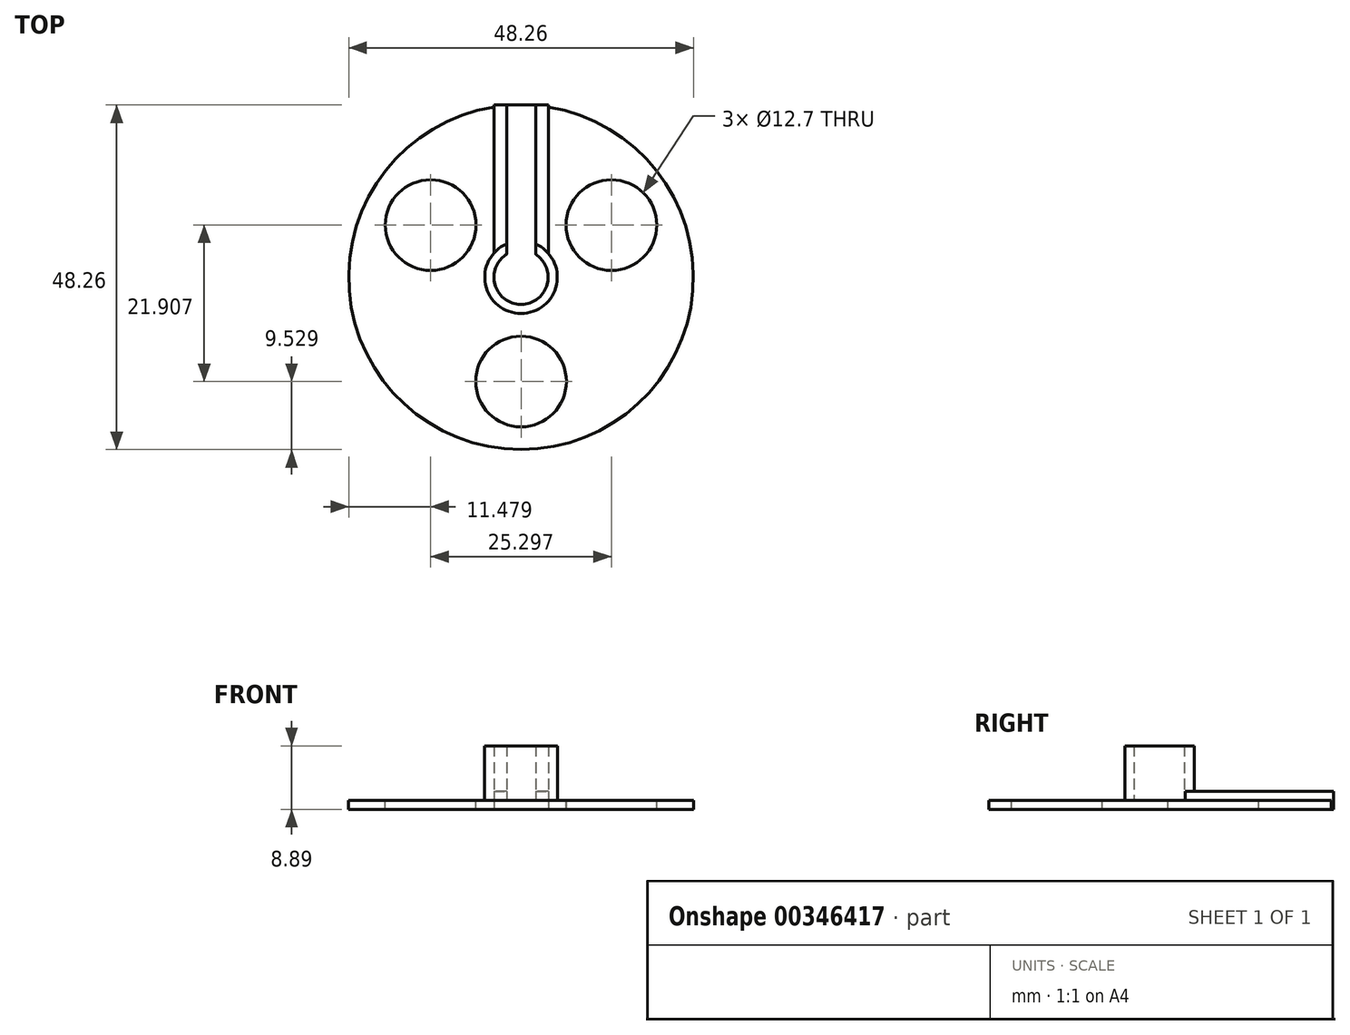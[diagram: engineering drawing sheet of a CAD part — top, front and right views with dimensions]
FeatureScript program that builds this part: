
annotation { "Feature Type Name" : "Feature", "Feature Type Description" : "" }
export const myFeature = defineFeature(function(context is Context, id is Id, definition is map)
    precondition{}
    {
        {
            var Q0;
            Q0=qCreatedBy(makeId("Top.planeOp"),FACE);
            var sketch = newSketch(context, id + "F0", { "sketchPlane" : qUnion([Q0])});
            skLineSegment(sketch, "E0.bottom", {"start": v(-94.86, 41.16) * mm, "end": v(-87.24, 41.16) * mm});
            skLineSegment(sketch, "E0.top", {"start": v(-94.86, 17.03) * mm, "end": v(-87.24, 17.03) * mm});
            skLineSegment(sketch, "E0.left", {"start": v(-94.86, 41.16) * mm, "end": v(-94.86, 17.03) * mm});
            skLineSegment(sketch, "E0.right", {"start": v(-87.24, 41.16) * mm, "end": v(-87.24, 17.03) * mm});
            skSolve(sketch);
        }
        {
            var Q0;
            Q0 = qSketchRegion(id + "F0", true);
            extrude(context, id + "F1", {"entities" : qUnion([Q0]), "depth" : 1.27 * mm});
        }
        {
            var Q0;
            Q0=makeQuery(id+"F1.opExtrude","CAP_FACE",FACE,{"disambiguationData":[OSD([sQuery(id+"F0.wireOp",EDGE,"E0.bottom"),sQuery(id+"F0.wireOp",EDGE,"E0.top"),sQuery(id+"F0.wireOp",EDGE,"E0.left"),sQuery(id+"F0.wireOp",EDGE,"E0.right")])],"isStart":false});
            var sketch = newSketch(context, id + "F2", { "sketchPlane" : qUnion([Q0])});
            skLineSegment(sketch, "E1.bottom", {"start": v(-94.86, 41.16) * mm, "end": v(-93.08, 41.16) * mm});
            skLineSegment(sketch, "E1.top", {"start": v(-94.86, 17.03) * mm, "end": v(-93.08, 17.03) * mm});
            skLineSegment(sketch, "E1.left", {"start": v(-94.86, 41.16) * mm, "end": v(-94.86, 17.03) * mm});
            skLineSegment(sketch, "E1.right", {"start": v(-93.08, 41.16) * mm, "end": v(-93.08, 17.03) * mm});
            skLineSegment(sketch, "E2.bottom", {"start": v(-87.24, 41.16) * mm, "end": v(-89.02, 41.16) * mm});
            skLineSegment(sketch, "E2.top", {"start": v(-87.24, 17.03) * mm, "end": v(-89.02, 17.03) * mm});
            skLineSegment(sketch, "E2.left", {"start": v(-87.24, 41.16) * mm, "end": v(-87.24, 17.03) * mm});
            skLineSegment(sketch, "E2.right", {"start": v(-89.02, 41.16) * mm, "end": v(-89.02, 17.03) * mm});
            skSolve(sketch);
        }
        {
            var Q0;
            Q0 = qSketchRegion(id + "F2", true);
            extrude(context, id + "F3", {"entities" : qUnion([Q0]), "operationType" : NewBodyOperationType.ADD, "depth" : 1.27 * mm});
        }
        {
            var Q0;
            Q0=makeQuery(id+"F1.opExtrude","CAP_FACE",FACE,{"disambiguationData":[OSD([sQuery(id+"F0.wireOp",EDGE,"E0.bottom"),sQuery(id+"F0.wireOp",EDGE,"E0.top"),sQuery(id+"F0.wireOp",EDGE,"E0.left"),sQuery(id+"F0.wireOp",EDGE,"E0.right")])],"isStart":false});
            var sketch = newSketch(context, id + "F4", { "sketchPlane" : qUnion([Q0])});
            skCircle(sketch, "E3", {"center": v(-91.05, 17.03) * mm, "radius": 5.08 * mm});
            skSolve(sketch);
        }
        {
            var Q0;
            Q0 = qSketchRegion(id + "F4", true);
            var Q1;
            Q1=makeQuery(id+"F1.opExtrude","CAP_FACE",FACE,{"disambiguationData":[OSD([sQuery(id+"F0.wireOp",EDGE,"E0.bottom"),sQuery(id+"F0.wireOp",EDGE,"E0.top"),sQuery(id+"F0.wireOp",EDGE,"E0.left"),sQuery(id+"F0.wireOp",EDGE,"E0.right")])],"isStart":true});
            extrude(context, id + "F5", {"entities" : qUnion([Q0]), "operationType" : NewBodyOperationType.ADD, "depth" : 7.62 * mm, "hasSecondDirection" : true, "secondDirectionBound" : SecondDirectionBoundingType.UP_TO_SURFACE, "secondDirectionOppositeDirection" : true, "secondDirectionBoundEntityFace" : qUnion([Q1]), "secondDirectionDepth" : 25.4 * mm});
        }
        {
            var Q0;
            Q0=makeQuery(id+"F5.opExtrude","CAP_FACE",FACE,{"disambiguationData":[OSD([sQuery(id+"F4.wireOp",EDGE,"E3")])],"isStart":false});
            shell(context, id + "F6", {"entities" : qUnion([Q0]), "thickness" : 1.27 * mm});
        }
        {
            var Q0;
            Q0=makeQuery(id+"F3.boolean.opBoolean","MERGE",FACE,{"derivedFrom":[makeQuery(id+"F1.opExtrude","SWEPT_FACE",FACE,{"disambiguationData":[OSD([sQuery(id+"F0.wireOp",EDGE,"E0.bottom")])]}),makeQuery(id+"F3.opExtrude","SWEPT_FACE",FACE,{"disambiguationData":[OSD([sQuery(id+"F2.wireOp",EDGE,"E1.bottom")])]}),makeQuery(id+"F3.opExtrude","SWEPT_FACE",FACE,{"disambiguationData":[OSD([sQuery(id+"F2.wireOp",EDGE,"E2.bottom")])]})]});
            var sketch = newSketch(context, id + "F7", { "sketchPlane" : qUnion([Q0])});
            skLineSegment(sketch, "E4.bottom", {"start": v(93.08, 2.54) * mm, "end": v(89.02, 2.54) * mm});
            skLineSegment(sketch, "E4.top", {"start": v(93.08, 1.27) * mm, "end": v(89.02, 1.27) * mm});
            skLineSegment(sketch, "E4.left", {"start": v(93.08, 2.54) * mm, "end": v(93.08, 1.27) * mm});
            skLineSegment(sketch, "E4.right", {"start": v(89.02, 2.54) * mm, "end": v(89.02, 1.27) * mm});
            skSolve(sketch);
        }
        {
            var Q0;
            Q0 = qSketchRegion(id + "F7", true);
            var Q1;
            {var subQ1=sQuery(id+"F2.wireOp",EDGE,"E1.top");var subQ2=sQuery(id+"F0.wireOp",EDGE,"E0.left");var subQ4=sQuery(id+"F0.wireOp",EDGE,"E0.top");Q1=makeQuery(id+"F5.boolean.opBoolean","SPLIT",FACE,{"disambiguationData":[TD([makeQuery(id+"F1.opExtrude","SWEPT_FACE",FACE,{"disambiguationData":[OSD([subQ2])]})])],"derivedFrom":makeQuery(id+"F3.boolean.opBoolean","MERGE",FACE,{"derivedFrom":[makeQuery(id+"F1.opExtrude","SWEPT_FACE",FACE,{"disambiguationData":[OSD([subQ4])]}),makeQuery(id+"F3.opExtrude","SWEPT_FACE",FACE,{"disambiguationData":[OSD([subQ1])]}),makeQuery(id+"F3.opExtrude","SWEPT_FACE",FACE,{"disambiguationData":[OSD([sQuery(id+"F2.wireOp",EDGE,"E2.top")])]})]})});}
            extrude(context, id + "F8", {"entities" : qUnion([Q0]), "operationType" : NewBodyOperationType.REMOVE, "oppositeDirection" : true, "endBoundEntityFace" : qUnion([Q1]), "depth" : 25.4 * mm});
        }
        {
            var Q0;
            Q0=makeQuery(id+"F3.boolean.opBoolean","MERGE",FACE,{"derivedFrom":[makeQuery(id+"F1.opExtrude","SWEPT_FACE",FACE,{"disambiguationData":[OSD([sQuery(id+"F0.wireOp",EDGE,"E0.bottom")])]}),makeQuery(id+"F3.opExtrude","SWEPT_FACE",FACE,{"disambiguationData":[OSD([sQuery(id+"F2.wireOp",EDGE,"E1.bottom")])]}),makeQuery(id+"F3.opExtrude","SWEPT_FACE",FACE,{"disambiguationData":[OSD([sQuery(id+"F2.wireOp",EDGE,"E2.bottom")])]})]});
            cPlane(context, id + "F9", {"entities" : qUnion([Q0]), "cplaneType" : CPlaneType.OFFSET, "offset" : 20.57 * mm, "oppositeDirection" : true, "width" : 152.4 * mm, "height" : 152.4 * mm});
        }
        {
            var Q0;
            Q0=qCreatedBy(id+"F9.planeOp",FACE);
            var sketch = newSketch(context, id + "F10", { "sketchPlane" : qUnion([Q0])});
            skLineSegment(sketch, "E5.0", {"start": v(89.02, 2.54) * mm, "end": v(93.08, 2.54) * mm});
            skArc(sketch, "E6", {"start": v(93.08, 2.54) * mm, "mid": v(91.05, 4.16) * mm, "end": v(89.02, 2.54) * mm});
            skSolve(sketch);
        }
        {
            var Q0;
            Q0 = qSketchRegion(id + "F10", true);
            extrude(context, id + "F11", {"entities" : qUnion([Q0]), "operationType" : NewBodyOperationType.REMOVE, "oppositeDirection" : true, "depth" : 2.54 * mm, "hasSecondDirection" : true, "secondDirectionOppositeDirection" : false, "secondDirectionDepth" : 2.54 * mm});
        }
        {
            var Q0;
            Q0=makeQuery(id+"F11.boolean.opBoolean","INTERSECT",EDGE,{"derivedFrom":[makeQuery(id+"F6.opShell","OFFSET_FACE",FACE,{"disambiguationData":[OSD([sQuery(id+"F4.wireOp",EDGE,"E3")])]}),makeQuery(id+"F11.opExtrude","SWEPT_FACE",FACE,{"disambiguationData":[OSD([sQuery(id+"F10.wireOp",EDGE,"E6")])]})]});
            fillet(context, id + "F12", {"entities" : qUnion([Q0]), "radius" : 2.54 * mm, "tangentPropagation" : true, "allowEdgeOverflow" : false});
        }
        {
            var Q0;
            Q0=makeQuery(id+"F5.boolean.opBoolean","MERGE",FACE,{"derivedFrom":[makeQuery(id+"F1.opExtrude","CAP_FACE",FACE,{"disambiguationData":[OSD([sQuery(id+"F0.wireOp",EDGE,"E0.bottom"),sQuery(id+"F0.wireOp",EDGE,"E0.top"),sQuery(id+"F0.wireOp",EDGE,"E0.left"),sQuery(id+"F0.wireOp",EDGE,"E0.right")])],"isStart":true}),makeQuery(id+"F5.opExtrude","CAP_FACE",FACE,{"disambiguationData":[OSD([sQuery(id+"F4.wireOp",EDGE,"E3")])],"isStart":true})]});
            var sketch = newSketch(context, id + "F13", { "sketchPlane" : qUnion([Q0])});
            skCircle(sketch, "E7", {"center": v(-91.05, -17.03) * mm, "radius": 24.13 * mm});
            skSolve(sketch);
        }
        {
            var Q0;
            Q0 = qSketchRegion(id + "F13", true);
            extrude(context, id + "F14", {"entities" : qUnion([Q0]), "operationType" : NewBodyOperationType.ADD, "oppositeDirection" : true, "depth" : 1.27 * mm});
        }
        {
            var Q0;
            Q0=makeQuery(id+"F14.opExtrude","CAP_FACE",FACE,{"disambiguationData":[OSD([sQuery(id+"F13.wireOp",EDGE,"E7")])],"isStart":false});
            var sketch = newSketch(context, id + "F15", { "sketchPlane" : qUnion([Q0])});
            skLineSegment(sketch, "E8.0", {"start": v(-87.24, 20.4) * mm, "end": v(-87.24, 40.86) * mm});
            skLineSegment(sketch, "E9", {"start": v(-91.05, 11.95) * mm, "end": v(-91.05, -7.1) * mm});
            skCircle(sketch, "E10", {"center": v(-91.05, 2.43) * mm, "radius": 6.35 * mm});
            skCircle(sketch, "E11.1.0", {"center": v(-78.4, 24.34) * mm, "radius": 6.35 * mm});
            skCircle(sketch, "E11.2.0", {"center": v(-103.7, 24.34) * mm, "radius": 6.35 * mm});
            skPoint(sketch, "E11.center", {"position": v(-91.05, 17.03) * mm});
            skSolve(sketch);
        }
        {
            var Q0;
            {var subQ0=sQuery(id+"F15.wireOp",EDGE,"E10");var subQ1=sQuery(id+"F15.wireOp",EDGE,"E9");var subQ2=makeQuery(id+"F15.imprint","INTERSECT",VERTEX,{"disambiguationData":[OD(0.0)],"derivedFrom":[subQ1,subQ0]});Q0=makeQuery(id+"F15.imprint","IMPRINT",FACE,{"disambiguationData":[TD([[makeQuery(id+"F15.imprint","IMPRINT",EDGE,{"disambiguationData":[TD([[subQ2,-1.0]])],"derivedFrom":subQ1}),-1.0]])]});}
            var Q1;
            {var subQ0=sQuery(id+"F15.wireOp",EDGE,"E10");var subQ1=sQuery(id+"F15.wireOp",EDGE,"E9");var subQ2=makeQuery(id+"F15.imprint","INTERSECT",VERTEX,{"disambiguationData":[OD(0.0)],"derivedFrom":[subQ1,subQ0]});Q1=makeQuery(id+"F15.imprint","IMPRINT",FACE,{"disambiguationData":[TD([[makeQuery(id+"F15.imprint","IMPRINT",EDGE,{"disambiguationData":[TD([[subQ2,-1.0]])],"derivedFrom":subQ1}),1.0]])]});}
            var Q2;
            Q2=makeQuery(id+"F15.imprint","IMPRINT",FACE,{"disambiguationData":[TD([[makeQuery(id+"F15.imprint","IMPRINT",EDGE,{"derivedFrom":sQuery(id+"F15.wireOp",EDGE,"E11.1.0")}),1.0]])]});
            var Q3;
            Q3=makeQuery(id+"F15.imprint","IMPRINT",FACE,{"disambiguationData":[TD([[makeQuery(id+"F15.imprint","IMPRINT",EDGE,{"derivedFrom":sQuery(id+"F15.wireOp",EDGE,"E11.2.0")}),1.0]])]});
            extrude(context, id + "F16", {"entities" : qUnion([Q0, Q1, Q2, Q3]), "operationType" : NewBodyOperationType.REMOVE, "oppositeDirection" : true, "depth" : 25.4 * mm});
        }
        {
            var Q0;
            {var subQ0=sQuery(id+"F0.wireOp",EDGE,"E0.right");var subQ1=sQuery(id+"F0.wireOp",EDGE,"E0.left");var subQ2=sQuery(id+"F0.wireOp",EDGE,"E0.top");var subQ3=sQuery(id+"F0.wireOp",EDGE,"E0.bottom");Q0=makeQuery(id+"F8.boolean.opBoolean","MERGE",FACE,{"derivedFrom":[makeQuery(id+"F1.opExtrude","CAP_FACE",FACE,{"disambiguationData":[OSD([subQ3,subQ2,subQ1,subQ0])],"isStart":false}),makeQuery(id+"F6.opShell","OFFSET_FACE",FACE,{"disambiguationData":[OSD([subQ3,subQ2,subQ1,subQ0])]}),makeQuery(id+"F8.opExtrude","SWEPT_FACE",FACE,{"disambiguationData":[OSD([sQuery(id+"F7.wireOp",EDGE,"E4.top")])]})]});}
            extrude(context, id + "F17", {"entities" : qUnion([Q0]), "operationType" : NewBodyOperationType.REMOVE, "depth" : 25.4 * mm, "offsetDistance" : 25.4 * mm});
        }
    });
